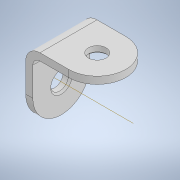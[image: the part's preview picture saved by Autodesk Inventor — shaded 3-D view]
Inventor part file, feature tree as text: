
AUTODESK INVENTOR PART (.ipt)
format: ipt  version: 2022 (Build 260153000, 153)  size: 145,920 bytes
history: native  units: mm
features: sketch x3, extrude x2, fillet x2, hole x1, plane x1, mirror x1, other x1, projected_geometry x1
ambient origin geometry x8: Origin, YZ Plane, XZ Plane, XY Plane, X Axis, Y Axis, Z Axis, Center Point
bodies: Solid1 (feature_tree)
feature tree (12):
  extrude  "Extrusion1"  Depth=20.066mm
  sketch  "Sketch2"  dims[d2=2.0mm d3=16.002mm d4=0.0mm]
  sketch  "Sketch5"  dims[d14=16.002mm d15=0.0mm d16=5.0mm d17=6.0mm d18=6.0mm d19=2.0mm d20=90.0deg d21=8.0mm d22=20.594885mm d23=4.0mm d24=2.0mm]
  extrude  "Extrusion3"  Depth=16.002mm TaperAngle=0.0deg
  hole  "Hole2"  [1 undecoded]
  plane  "Work Plane1"
  mirror  "Mirror1"
  other  "Work Axis1"
  fillet  "Fillet1"  Radius=2.0mm
  fillet  "Fillet2"  [1 undecoded]
  sketch  "Sketch1"  dims[d0=20.066mm d1=20.066mm]
  projected_geometry  "Projected Loop1"
note: 2 required parameter values undecoded (feature->parameter linkage not recoverable at this tier; creation-order binding heuristic only, values carry confidence <= 0.55)
